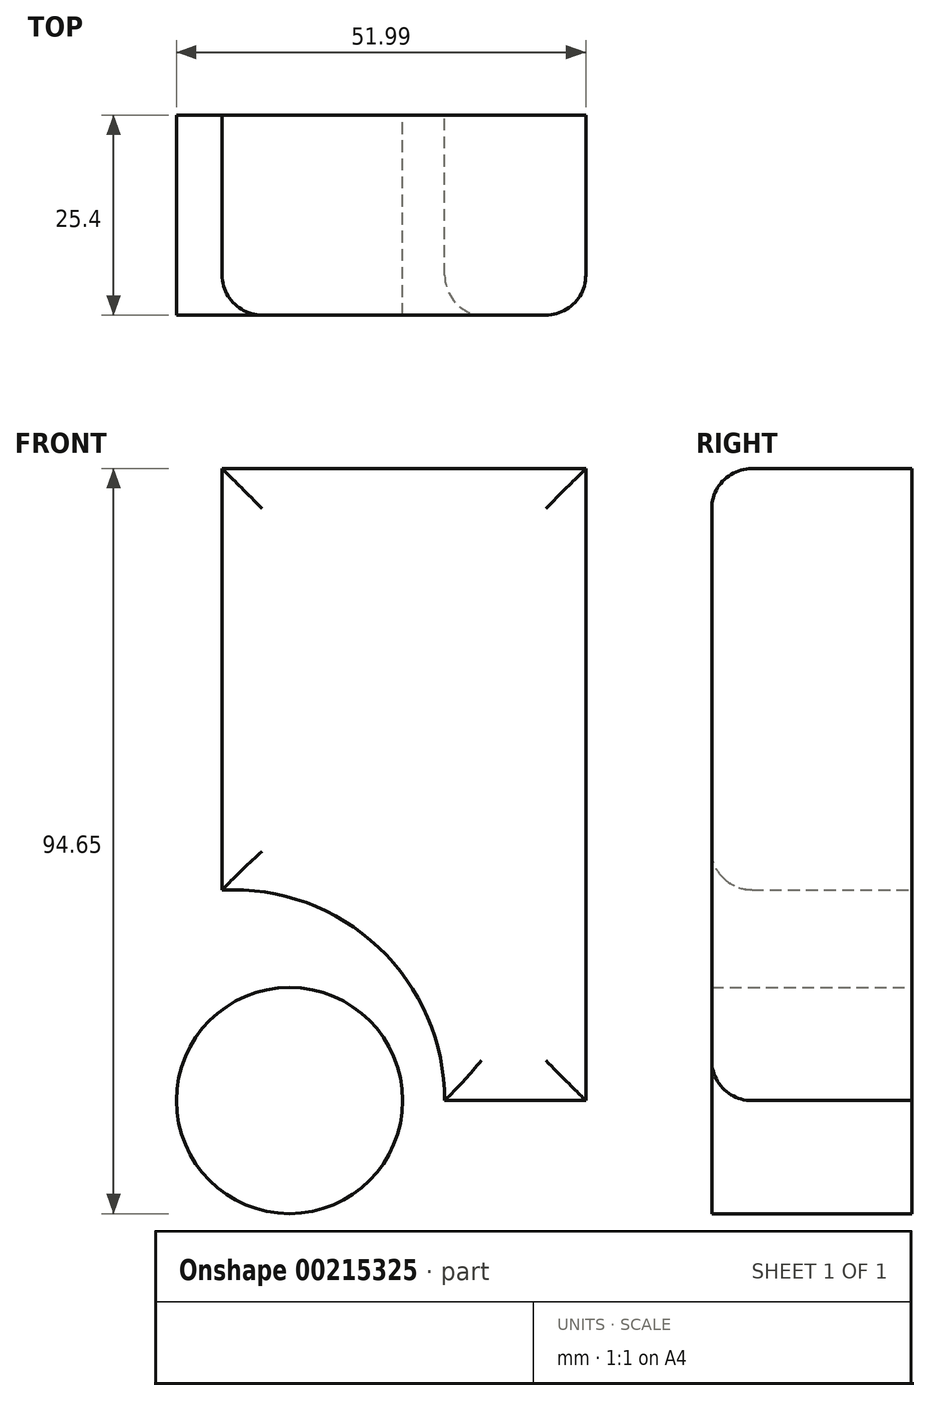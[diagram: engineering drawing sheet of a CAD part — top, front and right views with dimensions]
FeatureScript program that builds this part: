
annotation { "Feature Type Name" : "Feature", "Feature Type Description" : "" }
export const myFeature = defineFeature(function(context is Context, id is Id, definition is map)
    precondition{}
    {
        {
            var Q0;
            Q0=qCreatedBy(makeId("Front.planeOp"),FACE);
            var sketch = newSketch(context, id + "F0", { "sketchPlane" : qUnion([Q0])});
            skLineSegment(sketch, "E0.bottom", {"start": v(-24.22, 45.17) * mm, "end": v(21.98, 45.17) * mm});
            skLineSegment(sketch, "E0.top", {"start": v(4.05, -35.11) * mm, "end": v(21.98, -35.11) * mm});
            skLineSegment(sketch, "E0.left", {"start": v(-24.22, 45.17) * mm, "end": v(-24.22, -8.38) * mm});
            skLineSegment(sketch, "E0.right", {"start": v(21.98, 45.17) * mm, "end": v(21.98, -35.11) * mm});
            skArc(sketch, "E1", {"start": v(4.05, -35.11) * mm, "mid": v(-4.33, -15.66) * mm, "end": v(-24.22, -8.38) * mm});
            skCircle(sketch, "E2", {"center": v(-15.65, -35.11) * mm, "radius": 14.36 * mm});
            skSolve(sketch);
        }
        {
            var Q0;
            Q0 = qSketchRegion(id + "F0", true);
            extrude(context, id + "F1", {"entities" : qUnion([Q0]), "depth" : 25.4 * mm});
        }
        {
            var Q0;
            Q0=makeQuery(id+"F1.opExtrude","CAP_EDGE",EDGE,{"disambiguationData":[OSD([sQuery(id+"F0.wireOp",EDGE,"E0.left")])],"isStart":false});
            var Q1;
            Q1=makeQuery(id+"F1.opExtrude","CAP_EDGE",EDGE,{"disambiguationData":[OSD([sQuery(id+"F0.wireOp",EDGE,"E1")])],"isStart":false});
            var Q2;
            Q2=makeQuery(id+"F1.opExtrude","CAP_EDGE",EDGE,{"disambiguationData":[OSD([sQuery(id+"F0.wireOp",EDGE,"E0.top")])],"isStart":false});
            var Q3;
            Q3=makeQuery(id+"F1.opExtrude","CAP_EDGE",EDGE,{"disambiguationData":[OSD([sQuery(id+"F0.wireOp",EDGE,"E0.right")])],"isStart":false});
            var Q4;
            Q4=makeQuery(id+"F1.opExtrude","CAP_EDGE",EDGE,{"disambiguationData":[OSD([sQuery(id+"F0.wireOp",EDGE,"E0.bottom")])],"isStart":false});
            fillet(context, id + "F2", {"entities" : qUnion([Q0, Q1, Q2, Q3, Q4]), "radius" : 5.08 * mm, "tangentPropagation" : true, "allowEdgeOverflow" : false});
        }
    });
